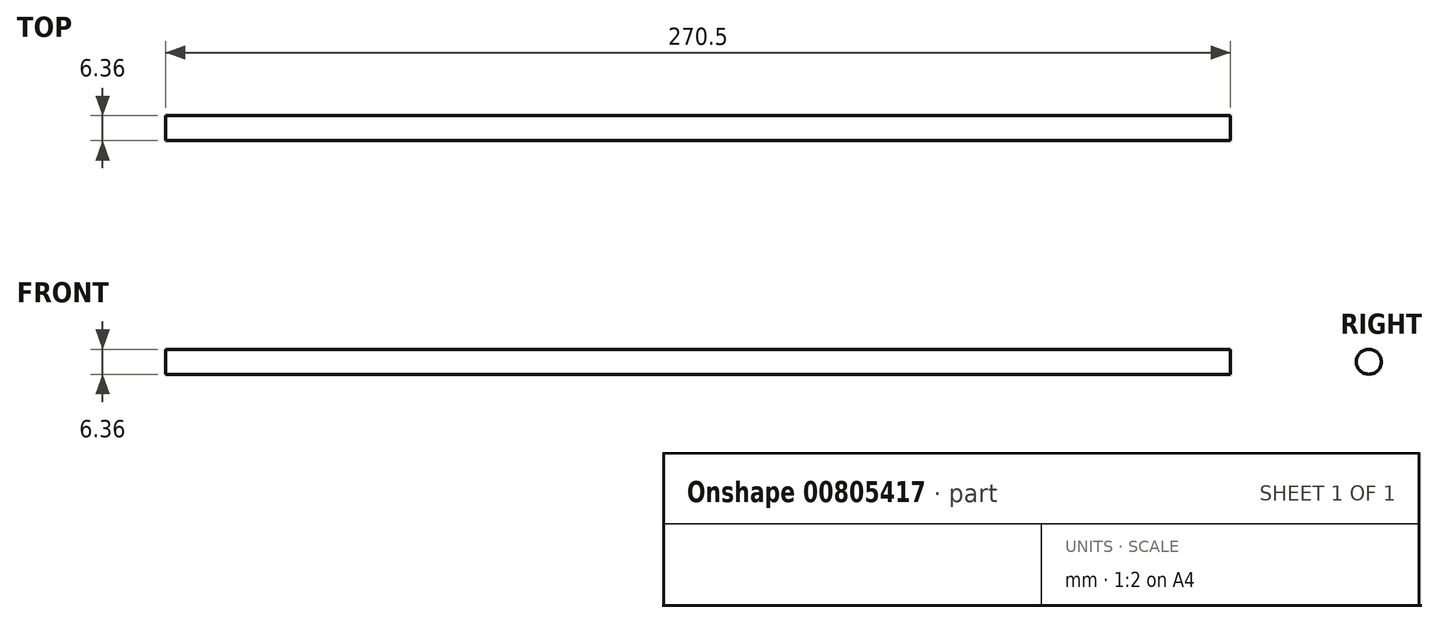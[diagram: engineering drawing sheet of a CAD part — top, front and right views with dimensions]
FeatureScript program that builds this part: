
annotation { "Feature Type Name" : "Feature", "Feature Type Description" : "" }
export const myFeature = defineFeature(function(context is Context, id is Id, definition is map)
    precondition{}
    {
        {
            var Q0;
            Q0=qCreatedBy(makeId("Right.planeOp"),FACE);
            var sketch = newSketch(context, id + "F0", { "sketchPlane" : qUnion([Q0])});
            skCircle(sketch, "E0", {"center": v(0, 0) * mm, "radius": 3.17 * mm});
            skSolve(sketch);
        }
        {
            var Q0;
            Q0 = qSketchRegion(id + "F0", true);
            extrude(context, id + "F1", {"entities" : qUnion([Q0]), "depth" : 270.5 * mm, "offsetDistance" : 25 * mm});
        }
    });
